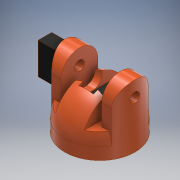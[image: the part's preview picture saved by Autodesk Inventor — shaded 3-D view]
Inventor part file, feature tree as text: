
AUTODESK INVENTOR PART (.ipt)
format: ipt  version: 2017 (Build 210142000, 142)  size: 252,928 bytes
history: native  units: mm
features: sketch x14, extrude x13, plane x9, revolve x1, mirror x1
ambient origin geometry x8: Origin, YZ Plane, XZ Plane, XY Plane, X Axis, Y Axis, Z Axis, Center Point
bodies: Solid1 (feature_tree)
feature tree (38):
  extrude  "Extrusion1"  Depth=18.0mm TaperAngle=0.0deg
  plane  "Work Plane1"
  revolve  "Revolution1"  Angle=90.0deg
  plane  "Work Plane3"
  extrude  "Extrusion5"  Depth=60.0mm TaperAngle=0.0deg
  sketch  "Sketch12"  dims[d35=18.0mm d36=0.0mm d37=18.0mm d38=0.0mm]
  extrude  "Extrusion6"  Depth=18.0mm TaperAngle=0.0deg
  extrude  "Extrusion7"  Depth=22.5mm TaperAngle=0.0deg
  extrude  "Extrusion8"  Depth=22.5mm TaperAngle=0.0deg
  plane  "Work Plane4"
  extrude  "Extrusion9"  [1 undecoded]
  extrude  "Extrusion10"  Depth=15.0mm
  sketch  "Sketch20"  dims[d57=22.5mm d58=0.0mm d60=15.0mm]
  plane  "Work Plane6"
  extrude  "Extrusion11"  Depth=60.0mm TaperAngle=0.0deg
  plane  "Work Plane7"
  extrude  "Extrusion12"  Depth=30.0mm TaperAngle=0.0deg
  plane  "Work Plane8"
  mirror  "Mirror1"
  plane  "Work Plane9"
  extrude  "Extrusion13"  [1 undecoded]
  extrude  "Extrusion14"  [1 undecoded]
  extrude  "Extrusion15"  [1 undecoded]
  plane  "Work Plane13"
  extrude  "Extrusion16"  [1 undecoded]
  sketch  "Sketch1"  dims[d0=107.0mm d1=18.0mm d2=0.0mm]
  sketch  "Sketch2"  dims[d3=0.0mm d4=90.0deg]
  plane  "Work Plane2"
  sketch  "Sketch11"  dims[d5=0.0mm d6=36.0mm d27=60.0mm d28=0.0mm]
  sketch  "Sketch13"  dims[d39=77.5mm d40=0.0mm d43=22.5mm d44=0.0mm]
  sketch  "Sketch18"  dims[d46=22.5mm d47=0.0mm d49=22.5mm d50=0.0mm]
  sketch  "Sketch19"  dims[d54=44.0mm d55=0.0mm d56=-22.0mm]
  sketch  "Sketch21"  dims[d61=72.2mm d65=60.0mm d66=0.0mm]
  sketch  "Sketch23"  dims[d70=13.0mm d71=0.0mm d75=30.0mm d76=0.0mm]
  sketch  "Sketch24"
  sketch  "Sketch27"
  sketch  "Sketch28"
  sketch  "Sketch29"
note: 5 required parameter values undecoded (feature->parameter linkage not recoverable at this tier; creation-order binding heuristic only, values carry confidence <= 0.55)
